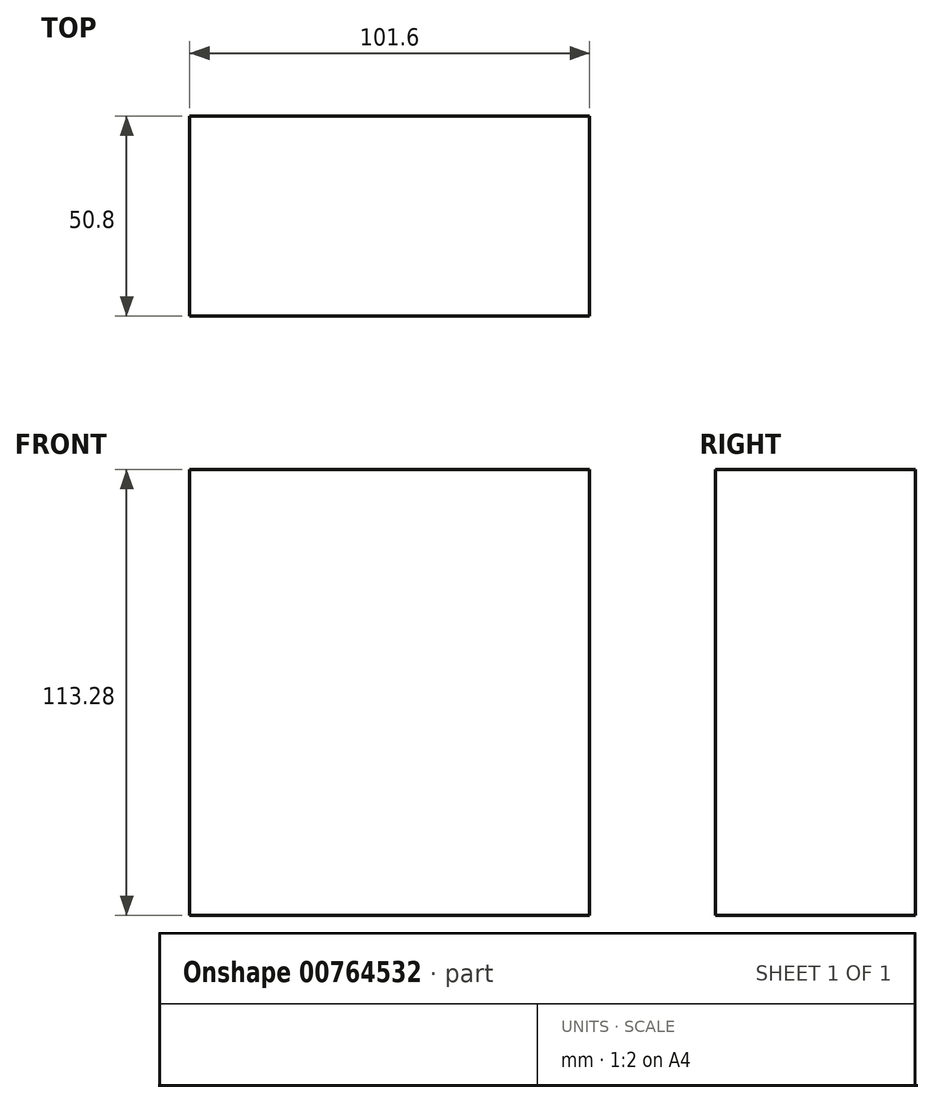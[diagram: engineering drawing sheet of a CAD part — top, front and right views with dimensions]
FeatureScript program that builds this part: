
annotation { "Feature Type Name" : "Feature", "Feature Type Description" : "" }
export const myFeature = defineFeature(function(context is Context, id is Id, definition is map)
    precondition{}
    {
        {
            var Q0;
            Q0=qCreatedBy(makeId("Top.planeOp"),FACE);
            var sketch = newSketch(context, id + "F0", { "sketchPlane" : qUnion([Q0])});
            skLineSegment(sketch, "E0.bottom", {"start": v(0, 0) * mm, "end": v(-101.6, 0) * mm});
            skLineSegment(sketch, "E0.top", {"start": v(0, 50.8) * mm, "end": v(-101.6, 50.8) * mm});
            skLineSegment(sketch, "E0.left", {"start": v(0, 0) * mm, "end": v(0, 50.8) * mm});
            skLineSegment(sketch, "E0.right", {"start": v(-101.6, 0) * mm, "end": v(-101.6, 50.8) * mm});
            skSolve(sketch);
        }
        {
            var Q0;
            Q0=makeQuery(id+"F0.imprint","IMPRINT",FACE,{"disambiguationData":[TD([[makeQuery(id+"F0.imprint","IMPRINT",EDGE,{"derivedFrom":sQuery(id+"F0.wireOp",EDGE,"E0.bottom")}),-1.0]])]});
            extrude(context, id + "F1", {"entities" : qUnion([Q0]), "depth" : 113.28 * mm, "offsetDistance" : 25.4 * mm});
        }
    });
